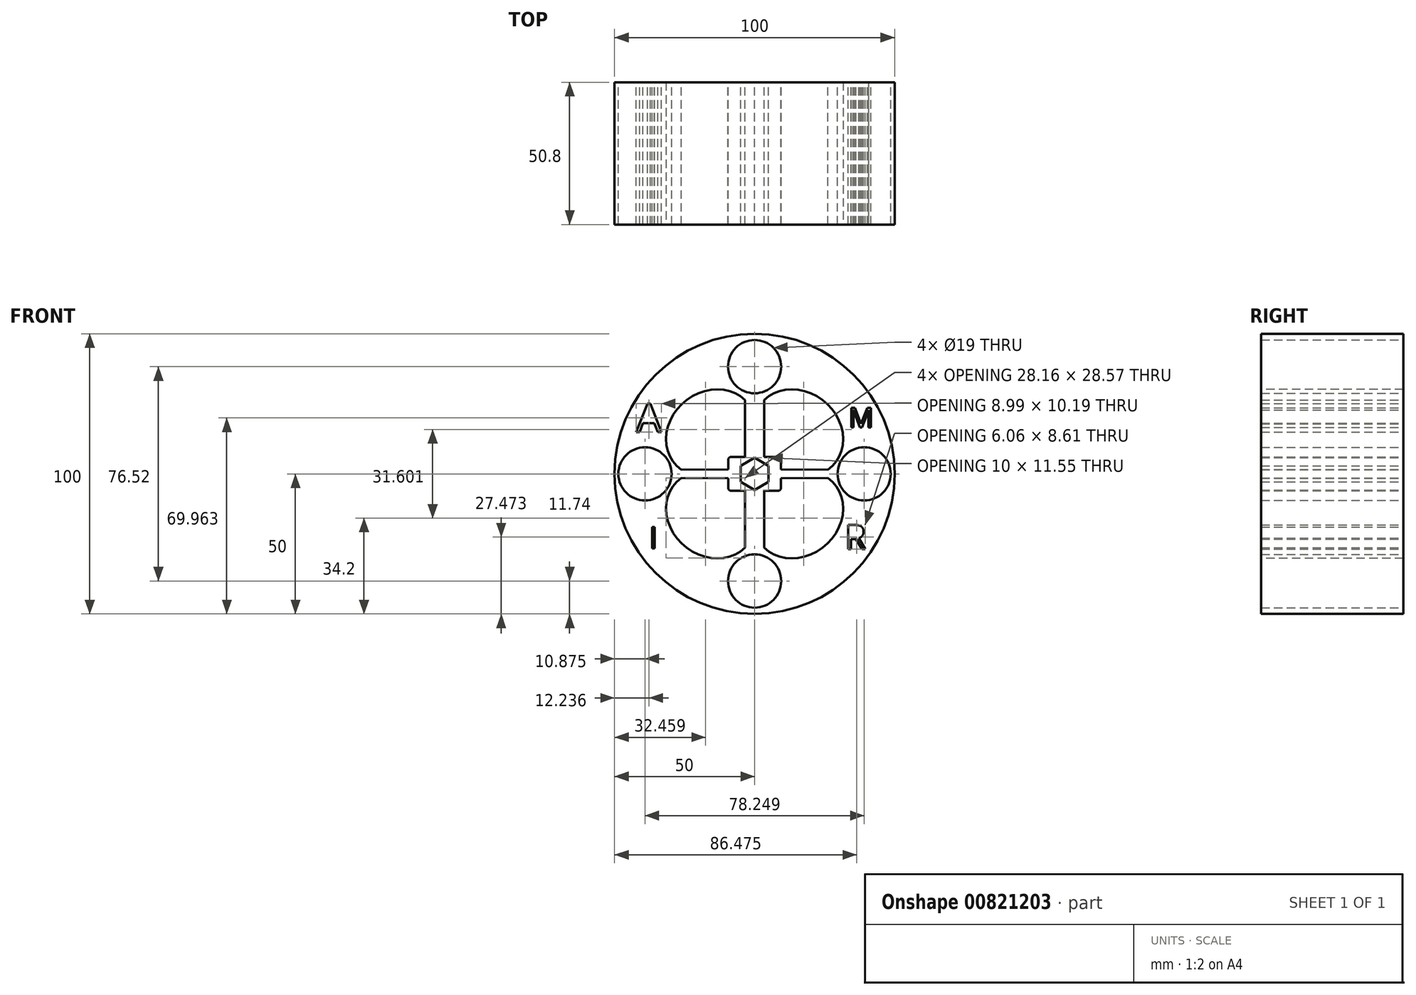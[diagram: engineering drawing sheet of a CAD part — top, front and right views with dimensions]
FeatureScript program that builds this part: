
annotation { "Feature Type Name" : "Feature", "Feature Type Description" : "" }
export const myFeature = defineFeature(function(context is Context, id is Id, definition is map)
    precondition{}
    {
        {
            var Q0;
            Q0=qCreatedBy(makeId("Front.planeOp"),FACE);
            var sketch = newSketch(context, id + "F0", { "sketchPlane" : qUnion([Q0])});
            skCircle(sketch, "E0", {"center": v(0, 0) * mm, "radius": 50 * mm});
            skCircle(sketch, "E1.cCircle", {"center": v(0, 0) * mm, "radius": 5 * mm, "construction": true});
            skLineSegment(sketch, "E1.0", {"start": v(5, 2.89) * mm, "end": v(5, -2.89) * mm});
            skLineSegment(sketch, "E1.1", {"start": v(5, -2.89) * mm, "end": v(0, -5.77) * mm});
            skLineSegment(sketch, "E1.2", {"start": v(0, -5.77) * mm, "end": v(-5, -2.89) * mm});
            skLineSegment(sketch, "E1.3", {"start": v(-5, -2.89) * mm, "end": v(-5, 2.89) * mm});
            skLineSegment(sketch, "E1.4", {"start": v(-5, 2.89) * mm, "end": v(0, 5.77) * mm});
            skLineSegment(sketch, "E1.5", {"start": v(0, 5.77) * mm, "end": v(5, 2.89) * mm});
            skPoint(sketch, "E1.0.midPoint", {"position": v(5, 0) * mm});
            skCircle(sketch, "E2", {"center": v(0, 38.26) * mm, "radius": 9.5 * mm});
            skCircle(sketch, "E3.MirrorC", {"center": v(0, -38.26) * mm, "radius": 9.5 * mm});
            skPoint(sketch, "E4.endSnap0", {"position": v(-2.5, 4.33) * mm});
            skPoint(sketch, "E4.end.orphan", {"position": v(-2.5, 10.03) * mm});
            skPoint(sketch, "E5.start.orphan", {"position": v(-9.3, 5.77) * mm});
            skPoint(sketch, "E6.end.orphan", {"position": v(25.63, -3.36) * mm});
            skPoint(sketch, "E7.end.orphan", {"position": v(25.63, 2.07) * mm});
            skPoint(sketch, "E8.start.orphan", {"position": v(22.77, 2.07) * mm});
            skPoint(sketch, "E9.center.orphan", {"position": v(-36.45, 0) * mm});
            skCircle(sketch, "E10", {"center": v(39.12, 0) * mm, "radius": 9.5 * mm});
            skCircle(sketch, "E11.MirrorC", {"center": v(-39.12, 0) * mm, "radius": 9.5 * mm});
            skLineSegment(sketch, "E12", {"start": v(3.1, 3.98) * mm, "end": v(3.1, 3.92) * mm});
            skPoint(sketch, "E13.visualSharp", {"position": v(-10.86, 1.24) * mm});
            skPoint(sketch, "E14.visualSharp", {"position": v(-9.45, -6.1) * mm});
            skPoint(sketch, "E15.end.orphan", {"position": v(-26.14, -1.58) * mm});
            skPoint(sketch, "E15.start.orphan", {"position": v(-10.86, -1.58) * mm});
            skPoint(sketch, "E16.MirrorCS.end.orphan", {"position": v(-2.5, -25.33) * mm});
            skPoint(sketch, "E16.MirrorCS.start.orphan", {"position": v(-2.5, -10.03) * mm});
            skPoint(sketch, "E17.start.orphan", {"position": v(-26.14, 1.24) * mm});
            skPoint(sketch, "E18.start.orphan", {"position": v(-9.3, 7.48) * mm});
            skPoint(sketch, "E19.start.orphan", {"position": v(-2.5, 25.33) * mm});
            skPoint(sketch, "E20.end.orphan", {"position": v(3.1, 25.33) * mm});
            skPoint(sketch, "E20.start.orphan", {"position": v(3.1, 10.03) * mm});
            skPoint(sketch, "E21.MirrorCS.end.orphan", {"position": v(26.14, 1.24) * mm});
            skPoint(sketch, "E21.MirrorCS.start.orphan", {"position": v(10.86, 1.24) * mm});
            skPoint(sketch, "E22.MirrorCS.end.orphan", {"position": v(26.14, -1.58) * mm});
            skPoint(sketch, "E22.MirrorCS.start.orphan", {"position": v(10.86, -1.58) * mm});
            skPoint(sketch, "E23.MirrorCS.end.orphan", {"position": v(3.1, -25.33) * mm});
            skPoint(sketch, "E23.MirrorCS.start.orphan", {"position": v(3.1, -10.03) * mm});
            skPoint(sketch, "E24.MirrorP", {"position": v(-9.45, 6.1) * mm});
            skEllipticalArc(sketch, "E25.MirrorCS", {});
            skLineSegment(sketch, "E26.MirrorCS", {"start": v(8.28, -6.1) * mm, "end": v(3.46, -6.1) * mm});
            skLineSegment(sketch, "E27.MirrorCS", {"start": v(3.46, -6.1) * mm, "end": v(3.46, -26.38) * mm});
            skArc(sketch, "E28.MirrorCS", {"start": v(9.45, -4.92) * mm, "mid": v(9.1, -5.75) * mm, "end": v(8.28, -6.1) * mm});
            skPoint(sketch, "E29.start.orphan", {"position": v(36.1, 26.5) * mm});
            skPoint(sketch, "E30.start.orphan", {"position": v(32.44, 26.5) * mm});
            skText(sketch, "E31", { "text": "R", "fontName": "OpenSans-Regular.ttf"});
            skText(sketch, "E32", { "text": "I\n", "fontName": "OpenSans-Regular.ttf"});
            skPoint(sketch, "E33.end.orphan", {"position": v(-37.17, 20.77) * mm});
            skPoint(sketch, "E34.start.orphan", {"position": v(-35.28, 32.47) * mm});
            skPoint(sketch, "E35.start.orphan", {"position": v(-33.74, 20.77) * mm});
            skPoint(sketch, "E36.start.orphan", {"position": v(-35.28, 28.38) * mm});
            skText(sketch, "E37", { "text": "A", "fontName": "OpenSans-Regular.ttf"});
            skPoint(sketch, "E38.end.orphan", {"position": v(35.99, 28.74) * mm});
            skPoint(sketch, "E39.start.orphan", {"position": v(37.71, 20.33) * mm});
            skPoint(sketch, "E40.end.orphan", {"position": v(32.44, 28.74) * mm});
            skPoint(sketch, "E41.start.orphan", {"position": v(31.03, 31.37) * mm});
            skPoint(sketch, "E42.start.orphan", {"position": v(35.38, 31.37) * mm});
            skPoint(sketch, "E43.end.orphan", {"position": v(31.03, 20.33) * mm});
            skPoint(sketch, "E43.start.orphan", {"position": v(32.44, 20.33) * mm});
            skText(sketch, "E44", { "text": "M", "fontName": "OpenSans-Regular.ttf"});
            skPoint(sketch, "E45.MirrorCS.end.orphan", {"position": v(-26.14, 1.58) * mm});
            skPoint(sketch, "E45.MirrorCS.start.orphan", {"position": v(-9.45, 1.12) * mm});
            skPoint(sketch, "E46.MirrorCS.end.orphan", {"position": v(-9.45, 4.92) * mm});
            skPoint(sketch, "E47.start.orphan", {"position": v(-9.45, -1.12) * mm});
            skPoint(sketch, "E48.MirrorCS.end.orphan", {"position": v(9.45, 4.92) * mm});
            skPoint(sketch, "E48.MirrorCS.start.orphan", {"position": v(9.45, 1.12) * mm});
            skPoint(sketch, "E49.MirrorCS.end.orphan", {"position": v(26.14, 1.58) * mm});
            skPoint(sketch, "E50.MirrorCS.end.orphan", {"position": v(9.45, -4.92) * mm});
            skPoint(sketch, "E50.MirrorCS.start.orphan", {"position": v(9.45, -1.12) * mm});
            skLineSegment(sketch, "E51", {"start": v(26.22, -1.51) * mm, "end": v(9.45, -1.58) * mm});
            skLineSegment(sketch, "E52", {"start": v(9.45, -1.58) * mm, "end": v(9.45, -4.92) * mm});
            skPoint(sketch, "E53.MirrorCS.end.orphan", {"position": v(3.46, 26.38) * mm});
            skPoint(sketch, "E53.MirrorCS.start.orphan", {"position": v(3.46, 6.1) * mm});
            skPoint(sketch, "E54.MirrorCS.start.orphan", {"position": v(8.28, 6.1) * mm});
            skPoint(sketch, "E55.end.orphan", {"position": v(9.45, 1.51) * mm});
            skPoint(sketch, "E56.MirrorCS.start.orphan", {"position": v(26.22, 1.51) * mm});
            skLineSegment(sketch, "E57.MirrorCS", {"start": v(26.22, 1.51) * mm, "end": v(9.45, 1.58) * mm});
            skEllipticalArc(sketch, "E58.MirrorCS", {});
            skLineSegment(sketch, "E59.MirrorCS", {"start": v(3.46, 6.1) * mm, "end": v(3.46, 26.38) * mm});
            skLineSegment(sketch, "E60.MirrorCS", {"start": v(8.28, 6.1) * mm, "end": v(3.46, 6.1) * mm});
            skLineSegment(sketch, "E61.MirrorCS", {"start": v(9.45, 1.58) * mm, "end": v(9.45, 4.92) * mm});
            skArc(sketch, "E62.MirrorCS", {"start": v(9.45, 4.92) * mm, "mid": v(9.1, 5.75) * mm, "end": v(8.28, 6.1) * mm});
            skPoint(sketch, "E63.MirrorCS.end.orphan", {"position": v(-3.46, 26.38) * mm});
            skPoint(sketch, "E63.MirrorCS.start.orphan", {"position": v(-3.46, 6.1) * mm});
            skPoint(sketch, "E64.MirrorCS.start.orphan", {"position": v(-8.28, 6.1) * mm});
            skPoint(sketch, "E65.end.orphan", {"position": v(-3.46, -26.38) * mm});
            skPoint(sketch, "E65.start.orphan", {"position": v(-3.46, -6.1) * mm});
            skPoint(sketch, "E66.start.orphan", {"position": v(-26.22, -1.51) * mm});
            skPoint(sketch, "E67.MirrorCS.end.orphan", {"position": v(-26.22, 1.51) * mm});
            skPoint(sketch, "E68.end.orphan", {"position": v(-9.45, -1.58) * mm});
            skPoint(sketch, "E14.filletArc.end.orphan", {"position": v(-8.28, -6.1) * mm});
            skPoint(sketch, "E14.filletArc.start.orphan", {"position": v(-9.45, -4.92) * mm});
            skLineSegment(sketch, "E69.MirrorCS", {"start": v(-3.46, 6.1) * mm, "end": v(-3.46, 26.38) * mm});
            skLineSegment(sketch, "E70.MirrorCS", {"start": v(-8.28, 6.1) * mm, "end": v(-3.46, 6.1) * mm});
            skLineSegment(sketch, "E71.MirrorCS", {"start": v(-9.45, 1.58) * mm, "end": v(-9.45, 4.92) * mm});
            skLineSegment(sketch, "E72.MirrorCS", {"start": v(-26.22, 1.51) * mm, "end": v(-9.45, 1.58) * mm});
            skEllipticalArc(sketch, "E73.MirrorCS", {});
            skLineSegment(sketch, "E74.MirrorCS", {"start": v(-26.22, -1.51) * mm, "end": v(-9.45, -1.58) * mm});
            skLineSegment(sketch, "E75.MirrorCS", {"start": v(-9.45, -1.58) * mm, "end": v(-9.45, -4.92) * mm});
            skEllipticalArc(sketch, "E76.MirrorCS", {});
            skLineSegment(sketch, "E77.MirrorCS", {"start": v(-3.46, -6.1) * mm, "end": v(-3.46, -26.38) * mm});
            skLineSegment(sketch, "E78.MirrorCS", {"start": v(-8.28, -6.1) * mm, "end": v(-3.46, -6.1) * mm});
            skArc(sketch, "E79.MirrorCS", {"start": v(-9.45, 4.92) * mm, "mid": v(-9.1, 5.75) * mm, "end": v(-8.28, 6.1) * mm});
            skArc(sketch, "E80.MirrorCS", {"start": v(-9.45, -4.92) * mm, "mid": v(-9.1, -5.75) * mm, "end": v(-8.28, -6.1) * mm});
            const initialGuessF0  = {"E25.MirrorCS": [0.015575654804706573, -0.014558497816324234, -0.7717082571345141, -0.6359767023015943, 0.01694377983366245, 0.014643182895431837, 0.09672092785218656, 3.3687528727316307], "E31": [0.03226, -0.02683, 1, 0, 0.00868], "E32": [-0.03768, -0.0266, 1, 0, 0.00773], "E37": [-0.04226, 0.01487, 1, 0, 0.01023], "E44": [0.03355, 0.01655, 1, 0, 0.00712], "E58.MirrorCS": [0.015575654804706573, 0.014558497816324234, -0.7717082571345141, 0.6359767023015943, 0.01694377983366245, 0.014643182895431837, 2.914432434447956, 6.1864643793274], "E73.MirrorCS": [-0.015575654804706573, 0.014558497816324234, 0.7717082571345141, 0.6359767023015943, 0.01694377983366245, 0.014643182895431837, 0.09672092785218656, 3.3687528727316303], "E76.MirrorCS": [-0.015575654804706573, -0.014558497816324234, 0.7717082571345141, -0.6359767023015943, 0.01694377983366245, 0.014643182895431837, 2.914432434447956, 6.1864643793274]};
            skSetInitialGuess(sketch, initialGuessF0);
            skSolve(sketch);
        }
        {
            var Q0;
            Q0 = qSketchRegion(id + "F0", true);
            extrude(context, id + "F1", {"entities" : qUnion([Q0]), "depth" : 50.8 * mm, "offsetDistance" : 25.4 * mm});
        }
    });
